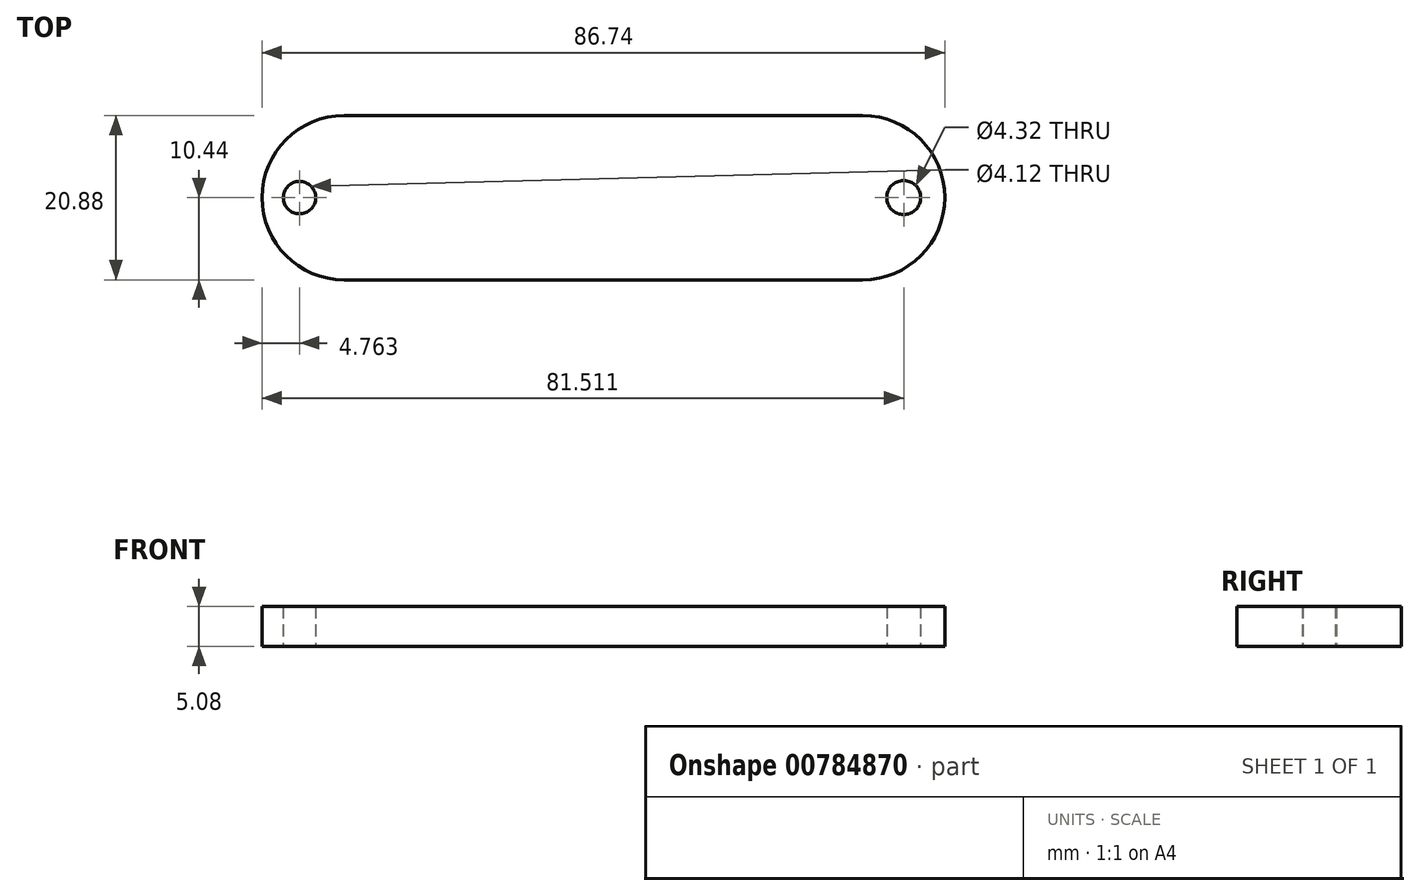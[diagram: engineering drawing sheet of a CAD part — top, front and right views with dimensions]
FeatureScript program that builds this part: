
annotation { "Feature Type Name" : "Feature", "Feature Type Description" : "" }
export const myFeature = defineFeature(function(context is Context, id is Id, definition is map)
    precondition{}
    {
        {
            var Q0;
            Q0=qCreatedBy(makeId("Top.planeOp"),FACE);
            var sketch = newSketch(context, id + "F0", { "sketchPlane" : qUnion([Q0])});
            skLineSegment(sketch, "E0.bottom", {"start": v(32.93, -10.44) * mm, "end": v(-32.93, -10.44) * mm});
            skLineSegment(sketch, "E0.top", {"start": v(32.93, 10.44) * mm, "end": v(-32.93, 10.44) * mm});
            skLineSegment(sketch, "E0.left", {"start": v(32.93, -10.44) * mm, "end": v(32.93, 10.44) * mm});
            skLineSegment(sketch, "E0.right", {"start": v(-32.93, -10.44) * mm, "end": v(-32.93, 10.44) * mm});
            skPoint(sketch, "E0.middle", {"position": v(0, 0) * mm});
            skArc(sketch, "E1", {"start": v(-32.93, 10.44) * mm, "mid": v(-43.37, 0) * mm, "end": v(-32.93, -10.44) * mm});
            skArc(sketch, "E2", {"start": v(32.93, -10.44) * mm, "mid": v(43.37, 0) * mm, "end": v(32.93, 10.44) * mm});
            skCircle(sketch, "E3", {"center": v(-38.6, 0) * mm, "radius": 2.06 * mm});
            skCircle(sketch, "E4", {"center": v(38.14, 0) * mm, "radius": 2.16 * mm});
            skSolve(sketch);
        }
        {
            var Q0;
            Q0=makeQuery(id+"F0.imprint","IMPRINT",FACE,{"disambiguationData":[TD([[makeQuery(id+"F0.imprint","IMPRINT",EDGE,{"derivedFrom":sQuery(id+"F0.wireOp",EDGE,"E0.bottom")}),-1.0]])]});
            var Q1;
            Q1=makeQuery(id+"F0.imprint","IMPRINT",FACE,{"disambiguationData":[TD([[makeQuery(id+"F0.imprint","IMPRINT",EDGE,{"derivedFrom":sQuery(id+"F0.wireOp",EDGE,"E0.left")}),-1.0]])]});
            var Q2;
            Q2=makeQuery(id+"F0.imprint","IMPRINT",FACE,{"disambiguationData":[TD([[makeQuery(id+"F0.imprint","IMPRINT",EDGE,{"derivedFrom":sQuery(id+"F0.wireOp",EDGE,"E0.right")}),1.0]])]});
            extrude(context, id + "F1", {"entities" : qUnion([Q0, Q1, Q2]), "depth" : 5.08 * mm, "offsetDistance" : 25.4 * mm});
        }
    });
